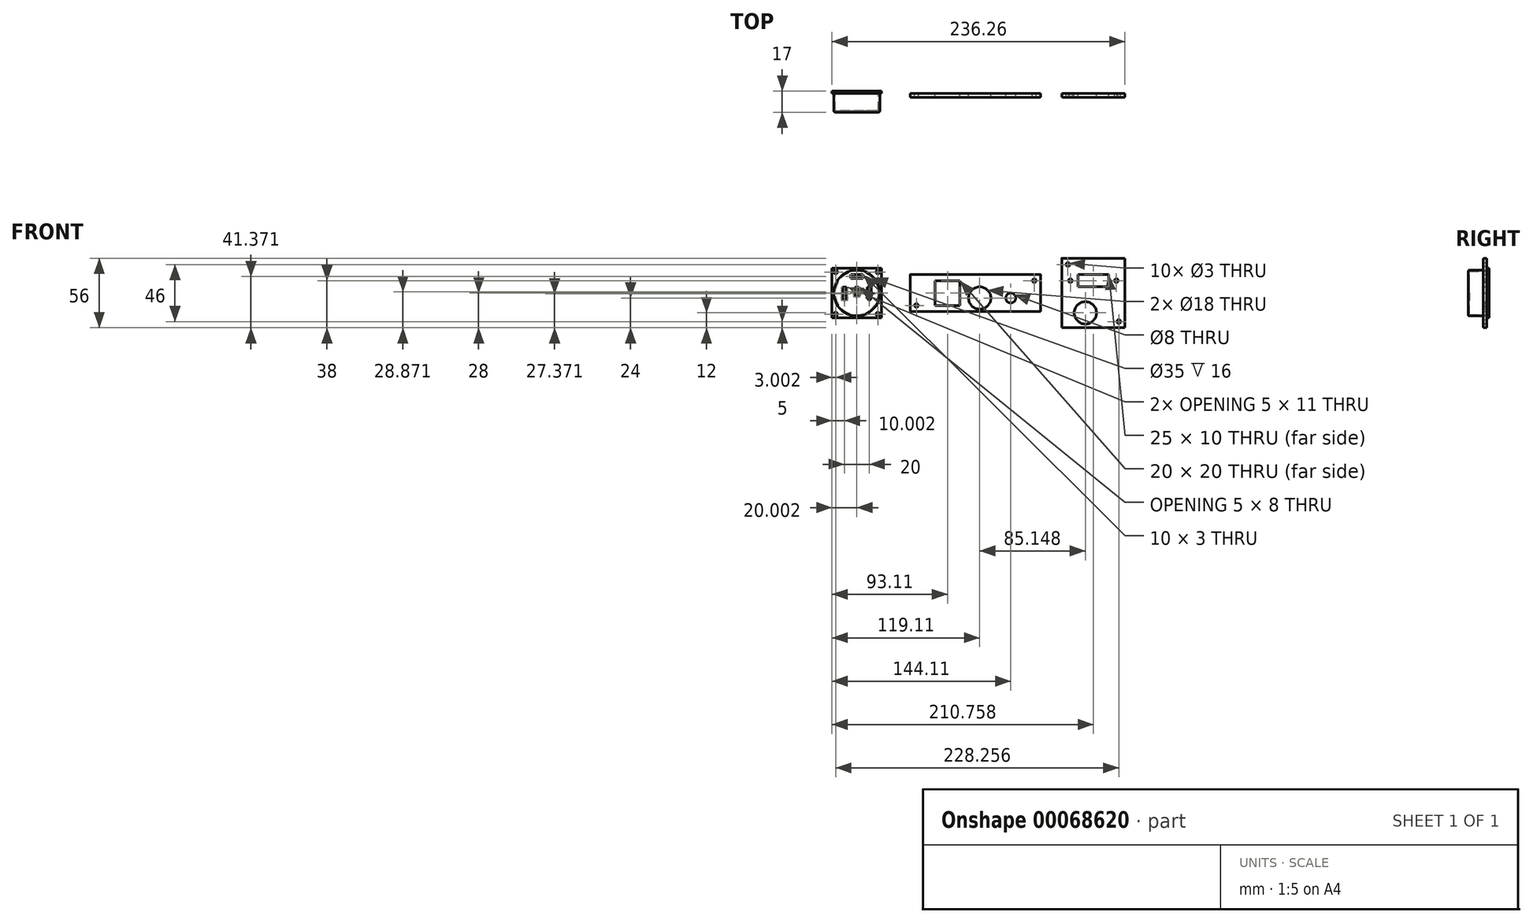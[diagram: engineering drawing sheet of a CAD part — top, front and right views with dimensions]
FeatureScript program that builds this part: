
annotation { "Feature Type Name" : "Feature", "Feature Type Description" : "" }
export const myFeature = defineFeature(function(context is Context, id is Id, definition is map)
    precondition{}
    {
        {
            var Q0;
            Q0=qCreatedBy(makeId("Front.planeOp"),FACE);
            var sketch = newSketch(context, id + "F0", { "sketchPlane" : qUnion([Q0])});
            skCircle(sketch, "E0", {"center": v(3.5, -4) * mm, "radius": 9 * mm});
            skLineSegment(sketch, "E1.bottom", {"start": v(-32.5, 10) * mm, "end": v(-12.5, 10) * mm});
            skLineSegment(sketch, "E1.top", {"start": v(-32.5, -10) * mm, "end": v(-12.5, -10) * mm});
            skLineSegment(sketch, "E1.left", {"start": v(-32.5, 10) * mm, "end": v(-32.5, -10) * mm});
            skLineSegment(sketch, "E1.right", {"start": v(-12.5, 10) * mm, "end": v(-12.5, -10) * mm});
            skCircle(sketch, "E2", {"center": v(28.5, -4) * mm, "radius": 4 * mm});
            skCircle(sketch, "E3", {"center": v(-47.5, -10) * mm, "radius": 1.5 * mm});
            skCircle(sketch, "E4", {"center": v(47.5, 10) * mm, "radius": 1.5 * mm});
            skLineSegment(sketch, "E5.bottom", {"start": v(52.5, -15) * mm, "end": v(-52.5, -15) * mm});
            skLineSegment(sketch, "E5.top", {"start": v(52.5, 15) * mm, "end": v(-52.5, 15) * mm});
            skLineSegment(sketch, "E5.left", {"start": v(52.5, -15) * mm, "end": v(52.5, 15) * mm});
            skLineSegment(sketch, "E5.right", {"start": v(-52.5, -15) * mm, "end": v(-52.5, 15) * mm});
            skPoint(sketch, "E5.middle", {"position": v(0, 0) * mm});
            skSolve(sketch);
        }
        {
            var Q0;
            Q0=makeQuery(id+"F0.imprint","IMPRINT",FACE,{"disambiguationData":[TD([[makeQuery(id+"F0.imprint","IMPRINT",EDGE,{"derivedFrom":sQuery(id+"F0.wireOp",EDGE,"E0")}),-1.0]])]});
            extrude(context, id + "F1", {"entities" : qUnion([Q0]), "depth" : 3 * mm});
        }
        {
            var Q0;
            Q0=makeQuery(id+"F1.opExtrude","CAP_EDGE",EDGE,{"disambiguationData":[OSD([sQuery(id+"F0.wireOp",EDGE,"E5.top")])],"isStart":false});
            var Q1;
            Q1=makeQuery(id+"F1.opExtrude","CAP_EDGE",EDGE,{"disambiguationData":[OSD([sQuery(id+"F0.wireOp",EDGE,"E5.right")])],"isStart":false});
            var Q2;
            Q2=makeQuery(id+"F1.opExtrude","CAP_EDGE",EDGE,{"disambiguationData":[OSD([sQuery(id+"F0.wireOp",EDGE,"E5.bottom")])],"isStart":false});
            var Q3;
            Q3=makeQuery(id+"F1.opExtrude","CAP_EDGE",EDGE,{"disambiguationData":[OSD([sQuery(id+"F0.wireOp",EDGE,"E5.left")])],"isStart":false});
            fillet(context, id + "F2", {"entities" : qUnion([Q0, Q1, Q2, Q3]), "radius" : 0.5 * mm, "tangentPropagation" : true, "allowEdgeOverflow" : false});
        }
        {
            var Q0;
            Q0=qCreatedBy(makeId("Front.planeOp"),FACE);
            var sketch = newSketch(context, id + "F3", { "sketchPlane" : qUnion([Q0])});
            skLineSegment(sketch, "E6.bottom", {"start": v(120.65, -28) * mm, "end": v(69.65, -28) * mm});
            skLineSegment(sketch, "E6.top", {"start": v(120.65, 28) * mm, "end": v(69.65, 28) * mm});
            skLineSegment(sketch, "E6.left", {"start": v(120.65, -28) * mm, "end": v(120.65, 28) * mm});
            skLineSegment(sketch, "E6.right", {"start": v(69.65, -28) * mm, "end": v(69.65, 28) * mm});
            skPoint(sketch, "E6.middle", {"position": v(95.15, 0) * mm});
            skCircle(sketch, "E7", {"center": v(74.65, 23) * mm, "radius": 1.5 * mm});
            skCircle(sketch, "E8", {"center": v(115.65, -23) * mm, "radius": 1.5 * mm});
            skCircle(sketch, "E9", {"center": v(88.65, -16) * mm, "radius": 9 * mm});
            skLineSegment(sketch, "E10.bottom", {"start": v(107.65, 5) * mm, "end": v(82.65, 5) * mm});
            skLineSegment(sketch, "E10.top", {"start": v(107.65, 15) * mm, "end": v(82.65, 15) * mm});
            skLineSegment(sketch, "E10.left", {"start": v(107.65, 5) * mm, "end": v(107.65, 15) * mm});
            skLineSegment(sketch, "E10.right", {"start": v(82.65, 5) * mm, "end": v(82.65, 15) * mm});
            skPoint(sketch, "E10.middle", {"position": v(95.15, 10) * mm});
            skCircle(sketch, "E11", {"center": v(76.65, 10) * mm, "radius": 1.5 * mm});
            skCircle(sketch, "E12", {"center": v(113.65, 10) * mm, "radius": 1.5 * mm});
            skSolve(sketch);
        }
        {
            var Q0;
            Q0 = qSketchRegion(id + "F3", true);
            extrude(context, id + "F4", {"entities" : qUnion([Q0]), "depth" : 3 * mm});
        }
        {
            var Q0;
            Q0=makeQuery(id+"F4.opExtrude","CAP_EDGE",EDGE,{"disambiguationData":[OSD([sQuery(id+"F3.wireOp",EDGE,"E6.top")])],"isStart":false});
            var Q1;
            Q1=makeQuery(id+"F4.opExtrude","CAP_EDGE",EDGE,{"disambiguationData":[OSD([sQuery(id+"F3.wireOp",EDGE,"E6.right")])],"isStart":false});
            var Q2;
            Q2=makeQuery(id+"F4.opExtrude","CAP_EDGE",EDGE,{"disambiguationData":[OSD([sQuery(id+"F3.wireOp",EDGE,"E6.left")])],"isStart":false});
            var Q3;
            Q3=makeQuery(id+"F4.opExtrude","CAP_EDGE",EDGE,{"disambiguationData":[OSD([sQuery(id+"F3.wireOp",EDGE,"E6.bottom")])],"isStart":false});
            fillet(context, id + "F5", {"entities" : qUnion([Q0, Q1, Q2, Q3]), "radius" : 1 * mm, "tangentPropagation" : true, "allowEdgeOverflow" : false});
        }
        {
            var Q0;
            Q0=qCreatedBy(makeId("Front.planeOp"),FACE);
            var sketch = newSketch(context, id + "F6", { "sketchPlane" : qUnion([Q0])});
            skCircle(sketch, "E13", {"center": v(-95.6, 0) * mm, "radius": 18.5 * mm});
            skSolve(sketch);
        }
        {
            var Q0;
            Q0 = qSketchRegion(id + "F6", true);
            extrude(context, id + "F7", {"entities" : qUnion([Q0]), "depth" : 15 * mm});
        }
        {
            var Q0;
            Q0=makeQuery(id+"F7.opExtrude","CAP_EDGE",EDGE,{"disambiguationData":[OSD([sQuery(id+"F6.wireOp",EDGE,"E13")])],"isStart":false});
            fillet(context, id + "F8", {"entities" : qUnion([Q0]), "radius" : 1 * mm, "tangentPropagation" : true, "allowEdgeOverflow" : false});
        }
        {
            var Q0;
            Q0=makeQuery(id+"F7.opExtrude","CAP_FACE",FACE,{"disambiguationData":[OSD([sQuery(id+"F6.wireOp",EDGE,"E13")])],"isStart":true});
            shell(context, id + "F9", {"entities" : qUnion([Q0]), "thickness" : 1 * mm});
        }
        {
            var Q0;
            Q0=makeQuery(id+"F7.opExtrude","CAP_FACE",FACE,{"disambiguationData":[OSD([sQuery(id+"F6.wireOp",EDGE,"E13"),sQuery(id+"F6.wireOp",EDGE,"Esf5itBe-Rekm-PuaR-I3QL-r79zV9LVYEKN.bottom"),sQuery(id+"F6.wireOp",EDGE,"Esf5itBe-Rekm-PuaR-I3QL-r79zV9LVYEKN.top"),sQuery(id+"F6.wireOp",EDGE,"Esf5itBe-Rekm-PuaR-I3QL-r79zV9LVYEKN.left"),sQuery(id+"F6.wireOp",EDGE,"Esf5itBe-Rekm-PuaR-I3QL-r79zV9LVYEKN.right"),sQuery(id+"F6.wireOp",EDGE,"0j1no3gY-SsaC-U71N-Fn9s-buFxBZ9oPYRc.top"),sQuery(id+"F6.wireOp",EDGE,"0j1no3gY-SsaC-U71N-Fn9s-buFxBZ9oPYRc.left"),sQuery(id+"F6.wireOp",EDGE,"0j1no3gY-SsaC-U71N-Fn9s-buFxBZ9oPYRc.right"),sQuery(id+"F6.wireOp",EDGE,"W482aUEI-9eq9-Mk7C-eVav-RZhC7vXtbm2Q"),sQuery(id+"F6.wireOp",EDGE,"a2hDfr64-Pp1r-tfV1-NXfD-V3pUvKYbAtsp"),sQuery(id+"F6.wireOp",EDGE,"u2XPa3WG-8BGT-asAA-Wqsa-QjbmhhXdVJUW"),sQuery(id+"F6.wireOp",EDGE,"EEjAVPfa-Werr-OgOK-M3jX-8QggiounJTzQ"),sQuery(id+"F6.wireOp",EDGE,"9719ca48-15b4-4f6b-9eaf-435dcdff279a.top"),sQuery(id+"F6.wireOp",EDGE,"9719ca48-15b4-4f6b-9eaf-435dcdff279a.left"),sQuery(id+"F6.wireOp",EDGE,"9719ca48-15b4-4f6b-9eaf-435dcdff279a.right"),sQuery(id+"F6.wireOp",EDGE,"ebb68154-9a52-4fc6-a236-d56a05d0ad4c"),sQuery(id+"F6.wireOp",EDGE,"eb26e9fb-7932-479b-9046-df3284eb59d3"),sQuery(id+"F6.wireOp",EDGE,"d9340d2b-f9cd-4749-837e-a9480a09c253"),sQuery(id+"F6.wireOp",EDGE,"5a250605-dac8-44e2-a521-55926b6bf676"),sQuery(id+"F6.wireOp",EDGE,"b6fd77d9-3516-4190-aba6-927b569a498c.top"),sQuery(id+"F6.wireOp",EDGE,"b6fd77d9-3516-4190-aba6-927b569a498c.left"),sQuery(id+"F6.wireOp",EDGE,"b6fd77d9-3516-4190-aba6-927b569a498c.right"),sQuery(id+"F6.wireOp",EDGE,"32018671-c3a3-447f-ad9f-cbfb8523262e"),sQuery(id+"F6.wireOp",EDGE,"b17abbf1-ba9c-4c67-9eff-51c833a29713"),sQuery(id+"F6.wireOp",EDGE,"6a737436-acba-4f85-915e-be7220d4c0c2"),sQuery(id+"F6.wireOp",EDGE,"b300f9e6-0503-4170-8434-b677de016588")])],"isStart":false});
            var sketch = newSketch(context, id + "F10", { "sketchPlane" : qUnion([Q0])});
            skLineSegment(sketch, "E14.bottom", {"start": v(-90.6, 11.87) * mm, "end": v(-100.6, 11.87) * mm});
            skLineSegment(sketch, "E14.top", {"start": v(-90.6, 14.87) * mm, "end": v(-100.6, 14.87) * mm});
            skLineSegment(sketch, "E14.left", {"start": v(-90.6, 11.87) * mm, "end": v(-90.6, 14.87) * mm});
            skLineSegment(sketch, "E14.right", {"start": v(-100.6, 11.87) * mm, "end": v(-100.6, 14.87) * mm});
            skPoint(sketch, "E14.middle", {"position": v(-95.6, 13.37) * mm});
            skLineSegment(sketch, "E15.top", {"start": v(-104.1, 4.87) * mm, "end": v(-107.1, 4.87) * mm});
            skLineSegment(sketch, "E15.left", {"start": v(-104.1, -3.13) * mm, "end": v(-104.1, 4.87) * mm});
            skLineSegment(sketch, "E15.right", {"start": v(-107.1, -3.13) * mm, "end": v(-107.1, 4.87) * mm});
            skPoint(sketch, "E15.middle", {"position": v(-105.6, 0.87) * mm});
            skLineSegment(sketch, "E16", {"start": v(-107.1, -3.13) * mm, "end": v(-108.1, -3.13) * mm});
            skLineSegment(sketch, "E17", {"start": v(-108.1, -3.13) * mm, "end": v(-105.6, -6.13) * mm});
            skLineSegment(sketch, "E18", {"start": v(-105.6, -6.13) * mm, "end": v(-103.1, -3.13) * mm});
            skLineSegment(sketch, "E19", {"start": v(-104.1, -3.13) * mm, "end": v(-103.1, -3.13) * mm});
            skLineSegment(sketch, "E20.top", {"start": v(-84.1, 4.87) * mm, "end": v(-87.1, 4.87) * mm});
            skLineSegment(sketch, "E20.left", {"start": v(-84.1, -3.13) * mm, "end": v(-84.1, 4.87) * mm});
            skLineSegment(sketch, "E20.right", {"start": v(-87.1, -3.13) * mm, "end": v(-87.1, 4.87) * mm});
            skPoint(sketch, "E20.middle", {"position": v(-85.6, 0.87) * mm});
            skLineSegment(sketch, "E21", {"start": v(-87.1, -3.13) * mm, "end": v(-88.1, -3.13) * mm});
            skLineSegment(sketch, "E22", {"start": v(-88.1, -3.13) * mm, "end": v(-85.6, -6.13) * mm});
            skLineSegment(sketch, "E23", {"start": v(-85.6, -6.13) * mm, "end": v(-83.1, -3.13) * mm});
            skLineSegment(sketch, "E24", {"start": v(-84.1, -3.13) * mm, "end": v(-83.1, -3.13) * mm});
            skLineSegment(sketch, "E25.top", {"start": v(-94.1, 4.87) * mm, "end": v(-97.1, 4.87) * mm});
            skLineSegment(sketch, "E25.left", {"start": v(-94.1, -0.13) * mm, "end": v(-94.1, 4.87) * mm});
            skLineSegment(sketch, "E25.right", {"start": v(-97.1, -0.13) * mm, "end": v(-97.1, 4.87) * mm});
            skPoint(sketch, "E25.middle", {"position": v(-95.6, 2.37) * mm});
            skLineSegment(sketch, "E26", {"start": v(-97.1, -0.13) * mm, "end": v(-98.1, -0.13) * mm});
            skLineSegment(sketch, "E27", {"start": v(-98.1, -0.13) * mm, "end": v(-95.6, -3.13) * mm});
            skLineSegment(sketch, "E28", {"start": v(-95.6, -3.13) * mm, "end": v(-93.1, -0.13) * mm});
            skLineSegment(sketch, "E29", {"start": v(-94.1, -0.13) * mm, "end": v(-93.1, -0.13) * mm});
            skSolve(sketch);
        }
        {
            var Q0;
            Q0 = qSketchRegion(id + "F10", true);
            extrude(context, id + "F11", {"entities" : qUnion([Q0]), "operationType" : NewBodyOperationType.REMOVE, "oppositeDirection" : true, "depth" : 1 * mm});
        }
        {
            var Q0;
            Q0=qCreatedBy(makeId("Front.planeOp"),FACE);
            var sketch = newSketch(context, id + "F12", { "sketchPlane" : qUnion([Q0])});
            skLineSegment(sketch, "E30.bottom", {"start": v(-75.6, -20) * mm, "end": v(-115.6, -20) * mm});
            skLineSegment(sketch, "E30.top", {"start": v(-75.6, 20) * mm, "end": v(-115.6, 20) * mm});
            skLineSegment(sketch, "E30.left", {"start": v(-75.6, -20) * mm, "end": v(-75.6, 20) * mm});
            skLineSegment(sketch, "E30.right", {"start": v(-115.6, -20) * mm, "end": v(-115.6, 20) * mm});
            skPoint(sketch, "E30.middle", {"position": v(-95.6, 0) * mm});
            skCircle(sketch, "E31", {"center": v(-95.6, 0) * mm, "radius": 17.5 * mm});
            skCircle(sketch, "E32", {"center": v(-112.6, 17) * mm, "radius": 1.5 * mm});
            skCircle(sketch, "E33", {"center": v(-78.6, 17) * mm, "radius": 1.5 * mm});
            skCircle(sketch, "E34", {"center": v(-78.6, -17) * mm, "radius": 1.5 * mm});
            skCircle(sketch, "E35", {"center": v(-112.6, -17) * mm, "radius": 1.5 * mm});
            skSolve(sketch);
        }
        {
            var Q0;
            Q0 = qSketchRegion(id + "F12", true);
            extrude(context, id + "F13", {"entities" : qUnion([Q0]), "operationType" : NewBodyOperationType.ADD, "oppositeDirection" : true, "depth" : 2 * mm});
        }
    });
